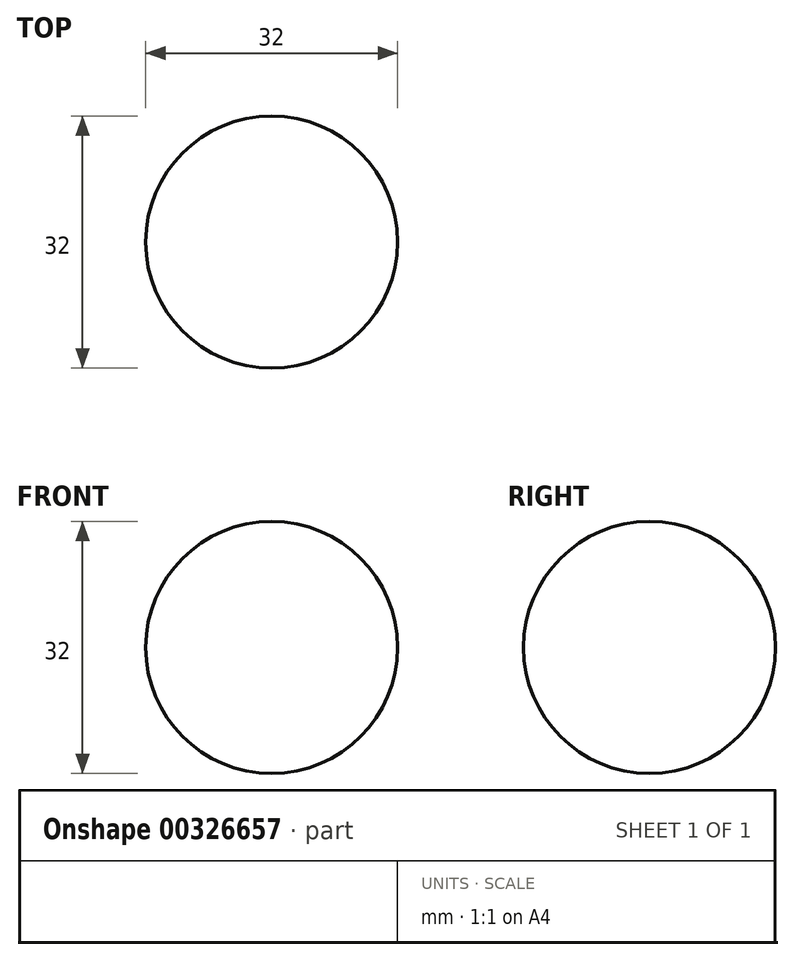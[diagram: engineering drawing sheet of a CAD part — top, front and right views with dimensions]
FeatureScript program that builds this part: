
annotation { "Feature Type Name" : "Feature", "Feature Type Description" : "" }
export const myFeature = defineFeature(function(context is Context, id is Id, definition is map)
    precondition{}
    {
        {
            var Q0;
            Q0=qCreatedBy(makeId("Front.planeOp"),FACE);
            var sketch = newSketch(context, id + "F0", { "sketchPlane" : qUnion([Q0])});
            skLineSegment(sketch, "E0", {"start": v(0, 0) * mm, "end": v(76.16, 0) * mm, "construction": true});
            skLineSegment(sketch, "E1", {"start": v(24.31, 0) * mm, "end": v(56.31, 0) * mm});
            skPoint(sketch, "E2", {"position": v(40.31, 0) * mm});
            skArc(sketch, "E3", {"start": v(56.31, 0) * mm, "mid": v(40.31, 16) * mm, "end": v(24.31, 0) * mm});
            skSolve(sketch);
        }
        {
            var Q0;
            Q0=makeQuery(id+"F0.imprint","IMPRINT",FACE,{"disambiguationData":[TD([[makeQuery(id+"F0.imprint","IMPRINT",EDGE,{"derivedFrom":sQuery(id+"F0.wireOp",EDGE,"E1")}),1.0]])]});
            var Q1;
            Q1=sQuery(id+"F0.wireOp",EDGE,"E1");
            revolve(context, id + "F1", {"entities" : qUnion([Q0]), "axis" : qUnion([Q1]), "revolveType" : RevolveType.FULL});
        }
    });
